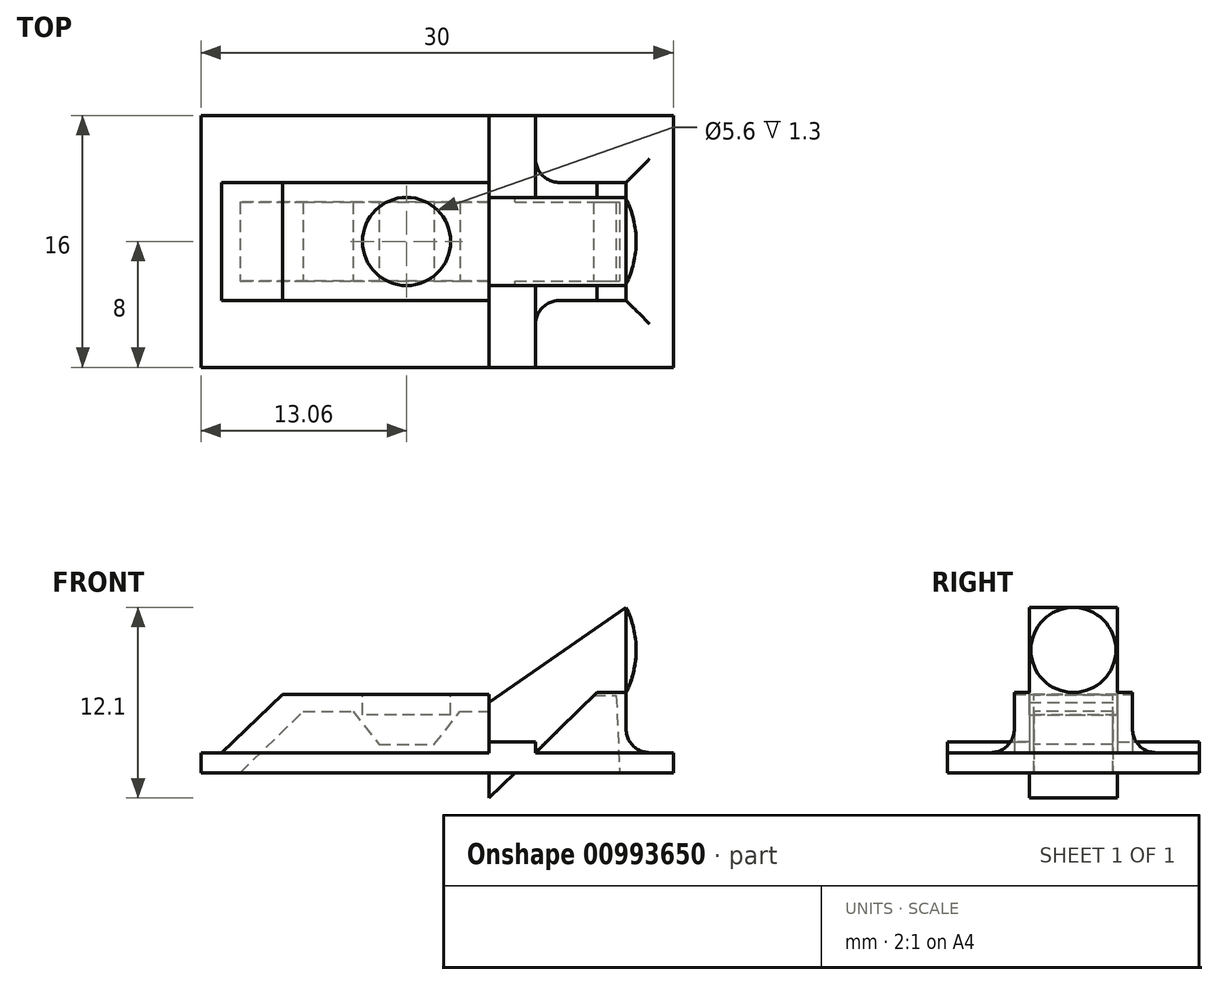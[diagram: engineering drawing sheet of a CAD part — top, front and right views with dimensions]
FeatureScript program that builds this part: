
annotation { "Feature Type Name" : "Feature", "Feature Type Description" : "" }
export const myFeature = defineFeature(function(context is Context, id is Id, definition is map)
    precondition{}
    {
        {
            var Q0;
            Q0=qCreatedBy(makeId("Top.planeOp"),FACE);
            var sketch = newSketch(context, id + "F0", { "sketchPlane" : qUnion([Q0])});
            skLineSegment(sketch, "E0", {"start": v(-16.66, 0) * mm, "end": v(17.96, 0) * mm, "construction": true});
            skLineSegment(sketch, "E1", {"start": v(0, 9.18) * mm, "end": v(0, -9.42) * mm, "construction": true});
            skLineSegment(sketch, "E2.bottom", {"start": v(-13.06, 8) * mm, "end": v(16.94, 8) * mm});
            skLineSegment(sketch, "E2.top", {"start": v(-13.06, -8) * mm, "end": v(16.94, -8) * mm});
            skLineSegment(sketch, "E2.left", {"start": v(-13.06, 8) * mm, "end": v(-13.06, -8) * mm});
            skLineSegment(sketch, "E2.right", {"start": v(16.94, 8) * mm, "end": v(16.94, -8) * mm});
            skSolve(sketch);
        }
        {
            var Q0;
            Q0=qSketchRegion(id+"F0",true);
            extrude(context, id + "F1", {"entities" : qUnion([Q0]), "depth" : 1.28 * mm, "offsetDistance" : 25 * mm});
        }
        {
            var Q0;
            Q0=qCreatedBy(makeId("Front.planeOp"),FACE);
            var sketch = newSketch(context, id + "F2", { "sketchPlane" : qUnion([Q0])});
            skLineSegment(sketch, "E3", {"start": v(-7.86, 4.98) * mm, "end": v(5.24, 4.98) * mm});
            skLineSegment(sketch, "E4", {"start": v(-7.86, 4.98) * mm, "end": v(-11.76, 1.28) * mm});
            skLineSegment(sketch, "E5", {"start": v(5.24, 4.98) * mm, "end": v(5.24, 1.28) * mm});
            skLineSegment(sketch, "E6", {"start": v(5.24, 1.28) * mm, "end": v(-11.76, 1.28) * mm});
            skSolve(sketch);
        }
        {
            var Q0;
            Q0=qSketchRegion(id+"F2",true);
            extrude(context, id + "F3", {"entities" : qUnion([Q0]), "operationType" : NewBodyOperationType.ADD, "endBound" : BoundingType.SYMMETRIC, "depth" : 7.5 * mm, "offsetDistance" : 25 * mm});
        }
        {
            var Q0;
            Q0=qCreatedBy(makeId("Front.planeOp"),FACE);
            var sketch = newSketch(context, id + "F4", { "sketchPlane" : qUnion([Q0])});
            skLineSegment(sketch, "E7.0", {"start": v(5.24, 4.48) * mm, "end": v(5.24, -1.6) * mm});
            skLineSegment(sketch, "E8", {"start": v(5.24, 4.48) * mm, "end": v(13.94, 10.5) * mm});
            skLineSegment(sketch, "E9", {"start": v(13.94, 5.1) * mm, "end": v(12.1, 5.1) * mm});
            skLineSegment(sketch, "E10", {"start": v(12.1, 5.1) * mm, "end": v(5.24, -1.6) * mm});
            skLineSegment(sketch, "E11", {"start": v(13.94, 10.5) * mm, "end": v(13.94, 5.1) * mm});
            skSolve(sketch);
        }
        {
            var Q0;
            Q0=qSketchRegion(id+"F4",true);
            extrude(context, id + "F5", {"entities" : qUnion([Q0]), "operationType" : NewBodyOperationType.ADD, "endBound" : BoundingType.SYMMETRIC, "depth" : 5.6 * mm, "offsetDistance" : 25 * mm});
        }
        {
            var Q0;
            Q0=qCreatedBy(makeId("Front.planeOp"),FACE);
            var sketch = newSketch(context, id + "F6", { "sketchPlane" : qUnion([Q0])});
            skLineSegment(sketch, "E12.0", {"start": v(12.1, 5.1) * mm, "end": v(6.88, 0) * mm});
            skLineSegment(sketch, "E13.0", {"start": v(13.94, 5.1) * mm, "end": v(12.1, 5.1) * mm});
            skLineSegment(sketch, "E14", {"start": v(13.94, 5.1) * mm, "end": v(13.94, 0) * mm});
            skLineSegment(sketch, "E15", {"start": v(13.94, 0) * mm, "end": v(6.88, 0) * mm});
            skSolve(sketch);
        }
        {
            var Q0;
            Q0=qSketchRegion(id+"F6",true);
            extrude(context, id + "F7", {"entities" : qUnion([Q0]), "operationType" : NewBodyOperationType.ADD, "endBound" : BoundingType.SYMMETRIC, "depth" : 7.5 * mm, "offsetDistance" : 25 * mm});
        }
        {
            var Q0;
            Q0=makeQuery(id+"F1.opExtrude","CAP_FACE",FACE,{"disambiguationData":[OSD([sQuery(id+"F0.wireOp",EDGE,"E2.bottom"),sQuery(id+"F0.wireOp",EDGE,"E2.top"),sQuery(id+"F0.wireOp",EDGE,"E2.left"),sQuery(id+"F0.wireOp",EDGE,"E2.right")])],"isStart":false});
            var sketch = newSketch(context, id + "F8", { "sketchPlane" : qUnion([Q0])});
            skLineSegment(sketch, "E16", {"start": v(8.18, -2.8) * mm, "end": v(8.18, -8) * mm});
            skLineSegment(sketch, "E17", {"start": v(8.18, -8) * mm, "end": v(5.24, -8) * mm});
            skLineSegment(sketch, "E18", {"start": v(5.24, -8) * mm, "end": v(5.24, -2.8) * mm});
            skLineSegment(sketch, "E19", {"start": v(5.24, -2.8) * mm, "end": v(8.18, -2.8) * mm});
            skLineSegment(sketch, "E20", {"start": v(5.24, 2.8) * mm, "end": v(5.24, 8) * mm});
            skLineSegment(sketch, "E21", {"start": v(5.24, 8) * mm, "end": v(8.18, 8) * mm});
            skLineSegment(sketch, "E22", {"start": v(8.18, 8) * mm, "end": v(8.18, 2.8) * mm});
            skLineSegment(sketch, "E23", {"start": v(8.18, 2.8) * mm, "end": v(5.24, 2.8) * mm});
            skSolve(sketch);
        }
        {
            var Q0;
            Q0=qSketchRegion(id+"F8",true);
            extrude(context, id + "F9", {"entities" : qUnion([Q0]), "operationType" : NewBodyOperationType.ADD, "depth" : 0.68 * mm, "offsetDistance" : 25 * mm});
        }
        {
            var Q0;
            Q0=makeQuery(id+"F3.opExtrude","SWEPT_EDGE",EDGE,{"disambiguationData":[OSD([sQuery(id+"F2.wireOp",EDGE,"E6"),sQuery(id+"F2.wireOp",EDGE,"LskEBJL7-cOJ8-ULC1-NJDM-6eLhHYPtE8pu")])]});
            var Q1;
            {var subQ0=sQuery(id+"F2.wireOp",EDGE,"E4");var subQ1=sQuery(id+"F2.wireOp",EDGE,"E6");Q1=makeQuery(id+"F9.boolean.opBoolean","SPLIT",EDGE,{"disambiguationData":[TD([makeQuery(id+"F3.opExtrude","SWEPT_FACE",FACE,{"disambiguationData":[OSD([subQ0])]})])],"derivedFrom":makeQuery(id+"F3.opExtrude","CAP_EDGE",EDGE,{"disambiguationData":[OSD([subQ1])],"isStart":false})});}
            var Q2;
            {var subQ0=sQuery(id+"F2.wireOp",EDGE,"LskEBJL7-cOJ8-ULC1-NJDM-6eLhHYPtE8pu");var subQ1=sQuery(id+"F2.wireOp",EDGE,"E6");Q2=makeQuery(id+"F9.boolean.opBoolean","SPLIT",EDGE,{"disambiguationData":[TD([makeQuery(id+"F3.opExtrude","SWEPT_FACE",FACE,{"disambiguationData":[OSD([subQ0])]})])],"derivedFrom":makeQuery(id+"F3.opExtrude","CAP_EDGE",EDGE,{"disambiguationData":[OSD([subQ1])],"isStart":false})});}
            var Q3;
            {var subQ0=sQuery(id+"F2.wireOp",EDGE,"E4");var subQ1=sQuery(id+"F2.wireOp",EDGE,"E6");Q3=makeQuery(id+"F9.boolean.opBoolean","SPLIT",EDGE,{"disambiguationData":[TD([makeQuery(id+"F3.opExtrude","SWEPT_FACE",FACE,{"disambiguationData":[OSD([subQ0])]})])],"derivedFrom":makeQuery(id+"F3.opExtrude","CAP_EDGE",EDGE,{"disambiguationData":[OSD([subQ1])],"isStart":true})});}
            var Q4;
            {var subQ0=sQuery(id+"F2.wireOp",EDGE,"LskEBJL7-cOJ8-ULC1-NJDM-6eLhHYPtE8pu");var subQ1=sQuery(id+"F2.wireOp",EDGE,"E6");Q4=makeQuery(id+"F9.boolean.opBoolean","SPLIT",EDGE,{"disambiguationData":[TD([makeQuery(id+"F3.opExtrude","SWEPT_FACE",FACE,{"disambiguationData":[OSD([subQ0])]})])],"derivedFrom":makeQuery(id+"F3.opExtrude","CAP_EDGE",EDGE,{"disambiguationData":[OSD([subQ1])],"isStart":true})});}
            var Q5;
            Q5=makeQuery(id+"F7.boolean.opBoolean","INTERSECT",EDGE,{"derivedFrom":[makeQuery(id+"F1.opExtrude","CAP_FACE",FACE,{"disambiguationData":[OSD([sQuery(id+"F0.wireOp",EDGE,"E2.bottom"),sQuery(id+"F0.wireOp",EDGE,"E2.top"),sQuery(id+"F0.wireOp",EDGE,"E2.left"),sQuery(id+"F0.wireOp",EDGE,"E2.right")])],"isStart":false}),makeQuery(id+"F7.opExtrude","CAP_FACE",FACE,{"disambiguationData":[OSD([sQuery(id+"F6.wireOp",EDGE,"E12.0"),sQuery(id+"F6.wireOp",EDGE,"E13.0"),sQuery(id+"F6.wireOp",EDGE,"E14"),sQuery(id+"F6.wireOp",EDGE,"E15")])],"isStart":false})]});
            var Q6;
            Q6=makeQuery(id+"F7.boolean.opBoolean","INTERSECT",EDGE,{"derivedFrom":[makeQuery(id+"F1.opExtrude","CAP_FACE",FACE,{"disambiguationData":[OSD([sQuery(id+"F0.wireOp",EDGE,"E2.bottom"),sQuery(id+"F0.wireOp",EDGE,"E2.top"),sQuery(id+"F0.wireOp",EDGE,"E2.left"),sQuery(id+"F0.wireOp",EDGE,"E2.right")])],"isStart":false}),makeQuery(id+"F7.opExtrude","SWEPT_FACE",FACE,{"disambiguationData":[OSD([sQuery(id+"F6.wireOp",EDGE,"E14")])]})]});
            var Q7;
            Q7=makeQuery(id+"F7.boolean.opBoolean","INTERSECT",EDGE,{"derivedFrom":[makeQuery(id+"F1.opExtrude","CAP_FACE",FACE,{"disambiguationData":[OSD([sQuery(id+"F0.wireOp",EDGE,"E2.bottom"),sQuery(id+"F0.wireOp",EDGE,"E2.top"),sQuery(id+"F0.wireOp",EDGE,"E2.left"),sQuery(id+"F0.wireOp",EDGE,"E2.right")])],"isStart":false}),makeQuery(id+"F7.opExtrude","CAP_FACE",FACE,{"disambiguationData":[OSD([sQuery(id+"F6.wireOp",EDGE,"E12.0"),sQuery(id+"F6.wireOp",EDGE,"E13.0"),sQuery(id+"F6.wireOp",EDGE,"E14"),sQuery(id+"F6.wireOp",EDGE,"E15")])],"isStart":true})]});
            fillet(context, id + "F10", {"entities" : qUnion([Q0, Q1, Q2, Q3, Q4, Q5, Q6, Q7]), "radius" : 1.5 * mm, "tangentPropagation" : true, "allowEdgeOverflow" : false});
        }
        {
            var Q0;
            Q0=makeQuery(id+"F3.opExtrude","SWEPT_FACE",FACE,{"disambiguationData":[OSD([sQuery(id+"F2.wireOp",EDGE,"E3")])]});
            var sketch = newSketch(context, id + "F11", { "sketchPlane" : qUnion([Q0])});
            skCircle(sketch, "E24", {"center": v(0, 0) * mm, "radius": 2.8 * mm});
            skSolve(sketch);
        }
        {
            var Q0;
            Q0=qSketchRegion(id+"F11",true);
            extrude(context, id + "F12", {"entities" : qUnion([Q0]), "operationType" : NewBodyOperationType.REMOVE, "oppositeDirection" : true, "depth" : 1.3 * mm, "offsetDistance" : 25 * mm});
        }
        {
            var Q0;
            Q0=qCreatedBy(makeId("Front.planeOp"),FACE);
            var sketch = newSketch(context, id + "F13", { "sketchPlane" : qUnion([Q0])});
            skLineSegment(sketch, "E25", {"start": v(-10.56, 0) * mm, "end": v(-6.56, 3.9) * mm});
            skLineSegment(sketch, "E26", {"start": v(-6.56, 3.9) * mm, "end": v(-3.41, 3.9) * mm});
            skLineSegment(sketch, "E27", {"start": v(-3.41, 3.9) * mm, "end": v(-1.75, 1.8) * mm});
            skLineSegment(sketch, "E28", {"start": v(-1.75, 1.8) * mm, "end": v(1.75, 1.8) * mm});
            skLineSegment(sketch, "E29", {"start": v(5.24, 0) * mm, "end": v(-10.56, 0) * mm});
            skLineSegment(sketch, "E30", {"start": v(6.88, 0) * mm, "end": v(11.89, 4.9) * mm});
            skLineSegment(sketch, "E31", {"start": v(11.89, 4.9) * mm, "end": v(13.32, 4.9) * mm});
            skLineSegment(sketch, "E32", {"start": v(13.32, 4.9) * mm, "end": v(13.54, 0) * mm});
            skLineSegment(sketch, "E33", {"start": v(6.88, 0) * mm, "end": v(13.54, 0) * mm});
            skLineSegment(sketch, "E34", {"start": v(1.75, 1.8) * mm, "end": v(3.41, 3.9) * mm});
            skLineSegment(sketch, "E35", {"start": v(3.41, 3.9) * mm, "end": v(5.24, 3.9) * mm});
            skLineSegment(sketch, "E36", {"start": v(5.24, 3.9) * mm, "end": v(5.24, 0) * mm});
            skLineSegment(sketch, "E37", {"start": v(0, 3.17) * mm, "end": v(0, -0.82) * mm, "construction": true});
            skSolve(sketch);
        }
        {
            var Q0;
            Q0=qSketchRegion(id+"F13",true);
            extrude(context, id + "F14", {"entities" : qUnion([Q0]), "operationType" : NewBodyOperationType.REMOVE, "endBound" : BoundingType.SYMMETRIC, "oppositeDirection" : true, "depth" : 5 * mm, "offsetDistance" : 25 * mm});
        }
        {
            var Q0;
            Q0=qCreatedBy(makeId("Front.planeOp"),FACE);
            var sketch = newSketch(context, id + "F15", { "sketchPlane" : qUnion([Q0])});
            skArc(sketch, "E38", {"start": v(14.58, 7.8) * mm, "mid": v(14.42, 9.19) * mm, "end": v(13.94, 10.5) * mm});
            skLineSegment(sketch, "E39", {"start": v(13.94, 10.5) * mm, "end": v(13.94, 7.8) * mm});
            skLineSegment(sketch, "E40", {"start": v(13.94, 7.8) * mm, "end": v(14.58, 7.8) * mm});
            skSolve(sketch);
        }
        {
            var Q0;
            Q0=qSketchRegion(id+"F15",true);
            var Q1;
            Q1=sQuery(id+"F15.wireOp",EDGE,"E40");
            revolve(context, id + "F16", {"operationType" : NewBodyOperationType.ADD, "surfaceOperationType" : NewSurfaceOperationType.NEW, "entities" : qUnion([Q0]), "axis" : qUnion([Q1]), "revolveType" : RevolveType.FULL});
        }
    });
